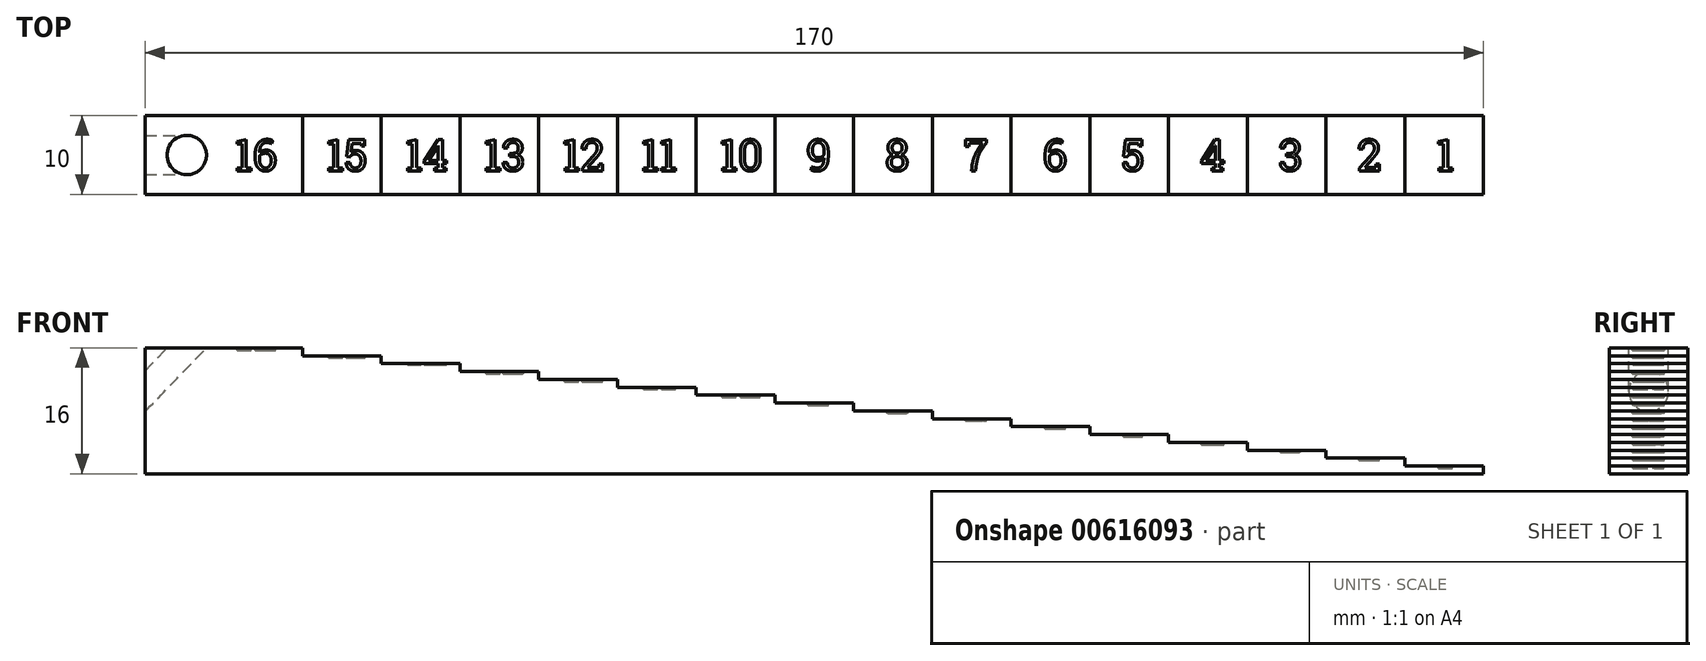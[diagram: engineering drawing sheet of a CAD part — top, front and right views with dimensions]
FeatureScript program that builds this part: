
annotation { "Feature Type Name" : "Feature", "Feature Type Description" : "" }
export const myFeature = defineFeature(function(context is Context, id is Id, definition is map)
    precondition{}
    {
        {
            var Q0;
            Q0=qCreatedBy(makeId("Front.planeOp"),FACE);
            var sketch = newSketch(context, id + "F0", { "sketchPlane" : qUnion([Q0])});
            skLineSegment(sketch, "E0", {"start": v(0, 0) * mm, "end": v(-170, 0) * mm});
            skLineSegment(sketch, "E1", {"start": v(-170, 0) * mm, "end": v(-170, 16) * mm});
            skLineSegment(sketch, "E2", {"start": v(0, 0) * mm, "end": v(0, 1) * mm});
            skLineSegment(sketch, "E3", {"start": v(0, 1) * mm, "end": v(-10, 1) * mm});
            skLineSegment(sketch, "E4", {"start": v(-10, 1) * mm, "end": v(-10, 2) * mm});
            skLineSegment(sketch, "E5", {"start": v(-10, 2) * mm, "end": v(-20, 2) * mm});
            skLineSegment(sketch, "E6", {"start": v(-20, 2) * mm, "end": v(-20, 3) * mm});
            skLineSegment(sketch, "E7", {"start": v(-20, 3) * mm, "end": v(-30, 3) * mm});
            skLineSegment(sketch, "E8", {"start": v(-30, 3) * mm, "end": v(-30, 4) * mm});
            skLineSegment(sketch, "E9", {"start": v(-30, 4) * mm, "end": v(-40, 4) * mm});
            skLineSegment(sketch, "E10", {"start": v(-40, 4) * mm, "end": v(-40, 5) * mm});
            skLineSegment(sketch, "E11", {"start": v(-40, 5) * mm, "end": v(-50, 5) * mm});
            skLineSegment(sketch, "E12", {"start": v(-50, 5) * mm, "end": v(-50, 6) * mm});
            skLineSegment(sketch, "E13", {"start": v(-50, 6) * mm, "end": v(-60, 6) * mm});
            skLineSegment(sketch, "E14", {"start": v(-60, 6) * mm, "end": v(-60, 7) * mm});
            skLineSegment(sketch, "E15", {"start": v(-60, 7) * mm, "end": v(-70, 7) * mm});
            skLineSegment(sketch, "E16", {"start": v(-70, 7) * mm, "end": v(-70, 8) * mm});
            skLineSegment(sketch, "E17", {"start": v(-70, 8) * mm, "end": v(-80, 8) * mm});
            skLineSegment(sketch, "E18", {"start": v(-80, 8) * mm, "end": v(-80, 9) * mm});
            skLineSegment(sketch, "E19", {"start": v(-80, 9) * mm, "end": v(-90, 9) * mm});
            skLineSegment(sketch, "E20", {"start": v(-90, 9) * mm, "end": v(-90, 10) * mm});
            skLineSegment(sketch, "E21", {"start": v(-90, 10) * mm, "end": v(-100, 10) * mm});
            skLineSegment(sketch, "E22", {"start": v(-100, 10) * mm, "end": v(-100, 11) * mm});
            skLineSegment(sketch, "E23", {"start": v(-100, 11) * mm, "end": v(-110, 11) * mm});
            skLineSegment(sketch, "E24", {"start": v(-110, 11) * mm, "end": v(-110, 12) * mm});
            skLineSegment(sketch, "E25", {"start": v(-110, 12) * mm, "end": v(-120, 12) * mm});
            skLineSegment(sketch, "E26", {"start": v(-120, 12) * mm, "end": v(-120, 13) * mm});
            skLineSegment(sketch, "E27", {"start": v(-120, 13) * mm, "end": v(-130, 13) * mm});
            skLineSegment(sketch, "E28", {"start": v(-130, 13) * mm, "end": v(-130, 14) * mm});
            skLineSegment(sketch, "E29", {"start": v(-130, 14) * mm, "end": v(-140, 14) * mm});
            skLineSegment(sketch, "E30", {"start": v(-140, 14) * mm, "end": v(-140, 15) * mm});
            skLineSegment(sketch, "E31", {"start": v(-140, 15) * mm, "end": v(-150, 15) * mm});
            skLineSegment(sketch, "E32", {"start": v(-150, 15) * mm, "end": v(-150, 16) * mm});
            skLineSegment(sketch, "E33", {"start": v(-150, 16) * mm, "end": v(-170, 16) * mm});
            skSolve(sketch);
        }
        {
            var Q0;
            Q0 = qSketchRegion(id + "F0", true);
            extrude(context, id + "F1", {"entities" : qUnion([Q0]), "depth" : 10 * mm, "offsetDistance" : 25 * mm});
        }
        {
            var Q0;
            Q0=makeQuery(id+"F1.opExtrude","SWEPT_FACE",FACE,{"disambiguationData":[OSD([sQuery(id+"F0.wireOp",EDGE,"E3")])]});
            var sketch = newSketch(context, id + "F2", { "sketchPlane" : qUnion([Q0])});
            skText(sketch, "E34", { "text": "1", "fontName": "RobotoSlab-Regular.ttf"});
            const initialGuessF2  = {"E34": [-0.006, -0.007, 1, 0, 0.004]};
            skSetInitialGuess(sketch, initialGuessF2);
            skSolve(sketch);
        }
        {
            var Q0;
            Q0 = qSketchRegion(id + "F2", true);
            extrude(context, id + "F3", {"entities" : qUnion([Q0]), "operationType" : NewBodyOperationType.REMOVE, "oppositeDirection" : true, "depth" : 0.3 * mm, "offsetDistance" : 25 * mm});
        }
        {
            var Q0;
            Q0=makeQuery(id+"F1.opExtrude","SWEPT_FACE",FACE,{"disambiguationData":[OSD([sQuery(id+"F0.wireOp",EDGE,"E5")])]});
            var sketch = newSketch(context, id + "F4", { "sketchPlane" : qUnion([Q0])});
            skText(sketch, "E35", { "text": "2", "fontName": "RobotoSlab-Regular.ttf"});
            const initialGuessF4  = {"E35": [-0.016, -0.007, 1, 0, 0.004]};
            skSetInitialGuess(sketch, initialGuessF4);
            skSolve(sketch);
        }
        {
            var Q0;
            Q0 = qSketchRegion(id + "F4", true);
            extrude(context, id + "F5", {"entities" : qUnion([Q0]), "operationType" : NewBodyOperationType.REMOVE, "oppositeDirection" : true, "depth" : 0.3 * mm, "offsetDistance" : 25 * mm});
        }
        {
            var Q0;
            Q0=makeQuery(id+"F1.opExtrude","SWEPT_FACE",FACE,{"disambiguationData":[OSD([sQuery(id+"F0.wireOp",EDGE,"E7")])]});
            var sketch = newSketch(context, id + "F6", { "sketchPlane" : qUnion([Q0])});
            skText(sketch, "E36", { "text": "3", "fontName": "RobotoSlab-Regular.ttf"});
            const initialGuessF6  = {"E36": [-0.026, -0.007, 1, 0, 0.004]};
            skSetInitialGuess(sketch, initialGuessF6);
            skSolve(sketch);
        }
        {
            var Q0;
            Q0 = qSketchRegion(id + "F6", true);
            extrude(context, id + "F7", {"entities" : qUnion([Q0]), "operationType" : NewBodyOperationType.REMOVE, "oppositeDirection" : true, "depth" : 0.3 * mm, "offsetDistance" : 25 * mm});
        }
        {
            var Q0;
            Q0=makeQuery(id+"F1.opExtrude","SWEPT_FACE",FACE,{"disambiguationData":[OSD([sQuery(id+"F0.wireOp",EDGE,"E9")])]});
            var sketch = newSketch(context, id + "F8", { "sketchPlane" : qUnion([Q0])});
            skText(sketch, "E37", { "text": "4", "fontName": "RobotoSlab-Regular.ttf"});
            const initialGuessF8  = {"E37": [-0.036, -0.007, 1, 0, 0.004]};
            skSetInitialGuess(sketch, initialGuessF8);
            skSolve(sketch);
        }
        {
            var Q0;
            Q0 = qSketchRegion(id + "F8", true);
            extrude(context, id + "F9", {"entities" : qUnion([Q0]), "operationType" : NewBodyOperationType.REMOVE, "oppositeDirection" : true, "depth" : 0.3 * mm, "offsetDistance" : 25 * mm});
        }
        {
            var Q0;
            Q0=makeQuery(id+"F1.opExtrude","SWEPT_FACE",FACE,{"disambiguationData":[OSD([sQuery(id+"F0.wireOp",EDGE,"E11")])]});
            var sketch = newSketch(context, id + "F10", { "sketchPlane" : qUnion([Q0])});
            skText(sketch, "E38", { "text": "5", "fontName": "RobotoSlab-Regular.ttf"});
            const initialGuessF10  = {"E38": [-0.046, -0.007, 1, 0, 0.004]};
            skSetInitialGuess(sketch, initialGuessF10);
            skSolve(sketch);
        }
        {
            var Q0;
            Q0 = qSketchRegion(id + "F10", true);
            extrude(context, id + "F11", {"entities" : qUnion([Q0]), "operationType" : NewBodyOperationType.REMOVE, "oppositeDirection" : true, "depth" : 0.3 * mm, "offsetDistance" : 25 * mm});
        }
        {
            var Q0;
            Q0=makeQuery(id+"F1.opExtrude","SWEPT_FACE",FACE,{"disambiguationData":[OSD([sQuery(id+"F0.wireOp",EDGE,"E13")])]});
            var sketch = newSketch(context, id + "F12", { "sketchPlane" : qUnion([Q0])});
            skText(sketch, "E39", { "text": "6", "fontName": "RobotoSlab-Regular.ttf"});
            const initialGuessF12  = {"E39": [-0.056, -0.007, 1, 0, 0.004]};
            skSetInitialGuess(sketch, initialGuessF12);
            skSolve(sketch);
        }
        {
            var Q0;
            Q0 = qSketchRegion(id + "F12", true);
            extrude(context, id + "F13", {"entities" : qUnion([Q0]), "operationType" : NewBodyOperationType.REMOVE, "oppositeDirection" : true, "depth" : 0.3 * mm, "offsetDistance" : 25 * mm});
        }
        {
            var Q0;
            Q0=makeQuery(id+"F1.opExtrude","SWEPT_FACE",FACE,{"disambiguationData":[OSD([sQuery(id+"F0.wireOp",EDGE,"E15")])]});
            var sketch = newSketch(context, id + "F14", { "sketchPlane" : qUnion([Q0])});
            skText(sketch, "E40", { "text": "7", "fontName": "RobotoSlab-Regular.ttf"});
            const initialGuessF14  = {"E40": [-0.066, -0.007, 1, 0, 0.004]};
            skSetInitialGuess(sketch, initialGuessF14);
            skSolve(sketch);
        }
        {
            var Q0;
            Q0 = qSketchRegion(id + "F14", true);
            extrude(context, id + "F15", {"entities" : qUnion([Q0]), "operationType" : NewBodyOperationType.REMOVE, "oppositeDirection" : true, "depth" : 0.3 * mm, "offsetDistance" : 25 * mm});
        }
        {
            var Q0;
            Q0=makeQuery(id+"F1.opExtrude","SWEPT_FACE",FACE,{"disambiguationData":[OSD([sQuery(id+"F0.wireOp",EDGE,"E17")])]});
            var sketch = newSketch(context, id + "F16", { "sketchPlane" : qUnion([Q0])});
            skText(sketch, "E41", { "text": "8", "fontName": "RobotoSlab-Regular.ttf"});
            const initialGuessF16  = {"E41": [-0.076, -0.007, 1, 0, 0.004]};
            skSetInitialGuess(sketch, initialGuessF16);
            skSolve(sketch);
        }
        {
            var Q0;
            Q0 = qSketchRegion(id + "F16", true);
            extrude(context, id + "F17", {"entities" : qUnion([Q0]), "operationType" : NewBodyOperationType.REMOVE, "oppositeDirection" : true, "depth" : 0.3 * mm, "offsetDistance" : 25 * mm});
        }
        {
            var Q0;
            Q0=makeQuery(id+"F1.opExtrude","SWEPT_FACE",FACE,{"disambiguationData":[OSD([sQuery(id+"F0.wireOp",EDGE,"E19")])]});
            var sketch = newSketch(context, id + "F18", { "sketchPlane" : qUnion([Q0])});
            skText(sketch, "E42", { "text": "9", "fontName": "RobotoSlab-Regular.ttf"});
            const initialGuessF18  = {"E42": [-0.086, -0.007, 1, 0, 0.004]};
            skSetInitialGuess(sketch, initialGuessF18);
            skSolve(sketch);
        }
        {
            var Q0;
            Q0 = qSketchRegion(id + "F18", true);
            extrude(context, id + "F19", {"entities" : qUnion([Q0]), "operationType" : NewBodyOperationType.REMOVE, "oppositeDirection" : true, "depth" : 0.3 * mm, "offsetDistance" : 25 * mm});
        }
        {
            var Q0;
            Q0=makeQuery(id+"F1.opExtrude","SWEPT_FACE",FACE,{"disambiguationData":[OSD([sQuery(id+"F0.wireOp",EDGE,"E21")])]});
            var sketch = newSketch(context, id + "F20", { "sketchPlane" : qUnion([Q0])});
            skText(sketch, "E43", { "text": "10", "fontName": "RobotoSlab-Regular.ttf"});
            const initialGuessF20  = {"E43": [-0.097, -0.007, 1, 0, 0.004]};
            skSetInitialGuess(sketch, initialGuessF20);
            skSolve(sketch);
        }
        {
            var Q0;
            Q0 = qSketchRegion(id + "F20", true);
            extrude(context, id + "F21", {"entities" : qUnion([Q0]), "operationType" : NewBodyOperationType.REMOVE, "oppositeDirection" : true, "depth" : 0.3 * mm, "offsetDistance" : 25 * mm});
        }
        {
            var Q0;
            Q0=makeQuery(id+"F1.opExtrude","SWEPT_FACE",FACE,{"disambiguationData":[OSD([sQuery(id+"F0.wireOp",EDGE,"E23")])]});
            var sketch = newSketch(context, id + "F22", { "sketchPlane" : qUnion([Q0])});
            skText(sketch, "E44", { "text": "11", "fontName": "RobotoSlab-Regular.ttf"});
            const initialGuessF22  = {"E44": [-0.107, -0.007, 1, 0, 0.004]};
            skSetInitialGuess(sketch, initialGuessF22);
            skSolve(sketch);
        }
        {
            var Q0;
            Q0 = qSketchRegion(id + "F22", true);
            extrude(context, id + "F23", {"entities" : qUnion([Q0]), "operationType" : NewBodyOperationType.REMOVE, "oppositeDirection" : true, "depth" : 0.3 * mm, "offsetDistance" : 25 * mm});
        }
        {
            var Q0;
            Q0=makeQuery(id+"F1.opExtrude","SWEPT_FACE",FACE,{"disambiguationData":[OSD([sQuery(id+"F0.wireOp",EDGE,"E25")])]});
            var sketch = newSketch(context, id + "F24", { "sketchPlane" : qUnion([Q0])});
            skText(sketch, "E45", { "text": "12", "fontName": "RobotoSlab-Regular.ttf"});
            const initialGuessF24  = {"E45": [-0.117, -0.007, 1, 0, 0.004]};
            skSetInitialGuess(sketch, initialGuessF24);
            skSolve(sketch);
        }
        {
            var Q0;
            Q0 = qSketchRegion(id + "F24", true);
            extrude(context, id + "F25", {"entities" : qUnion([Q0]), "operationType" : NewBodyOperationType.REMOVE, "oppositeDirection" : true, "depth" : 0.3 * mm, "offsetDistance" : 25 * mm});
        }
        {
            var Q0;
            Q0=makeQuery(id+"F1.opExtrude","SWEPT_FACE",FACE,{"disambiguationData":[OSD([sQuery(id+"F0.wireOp",EDGE,"E27")])]});
            var sketch = newSketch(context, id + "F26", { "sketchPlane" : qUnion([Q0])});
            skText(sketch, "E46", { "text": "13", "fontName": "RobotoSlab-Regular.ttf"});
            const initialGuessF26  = {"E46": [-0.127, -0.007, 1, 0, 0.004]};
            skSetInitialGuess(sketch, initialGuessF26);
            skSolve(sketch);
        }
        {
            var Q0;
            Q0 = qSketchRegion(id + "F26", true);
            extrude(context, id + "F27", {"entities" : qUnion([Q0]), "operationType" : NewBodyOperationType.REMOVE, "oppositeDirection" : true, "depth" : 0.3 * mm, "offsetDistance" : 25 * mm});
        }
        {
            var Q0;
            Q0=makeQuery(id+"F1.opExtrude","SWEPT_FACE",FACE,{"disambiguationData":[OSD([sQuery(id+"F0.wireOp",EDGE,"E29")])]});
            var sketch = newSketch(context, id + "F28", { "sketchPlane" : qUnion([Q0])});
            skText(sketch, "E47", { "text": "14", "fontName": "RobotoSlab-Regular.ttf"});
            const initialGuessF28  = {"E47": [-0.137, -0.007, 1, 0, 0.004]};
            skSetInitialGuess(sketch, initialGuessF28);
            skSolve(sketch);
        }
        {
            var Q0;
            Q0 = qSketchRegion(id + "F28", true);
            extrude(context, id + "F29", {"entities" : qUnion([Q0]), "operationType" : NewBodyOperationType.REMOVE, "oppositeDirection" : true, "depth" : 0.2 * mm, "offsetDistance" : 25 * mm});
        }
        {
            var Q0;
            Q0=makeQuery(id+"F1.opExtrude","SWEPT_FACE",FACE,{"disambiguationData":[OSD([sQuery(id+"F0.wireOp",EDGE,"E31")])]});
            var sketch = newSketch(context, id + "F30", { "sketchPlane" : qUnion([Q0])});
            skText(sketch, "E48", { "text": "15", "fontName": "RobotoSlab-Regular.ttf"});
            skPoint(sketch, "E48.secondSnap0", {"position": v(-141.7, -7.25) * mm});
            const initialGuessF30  = {"E48": [-0.147, -0.007, 1, 0, 0.004]};
            skSetInitialGuess(sketch, initialGuessF30);
            skSolve(sketch);
        }
        {
            var Q0;
            Q0 = qSketchRegion(id + "F30", true);
            extrude(context, id + "F31", {"entities" : qUnion([Q0]), "operationType" : NewBodyOperationType.REMOVE, "oppositeDirection" : true, "depth" : 0.3 * mm, "offsetDistance" : 25 * mm});
        }
        {
            var Q0;
            Q0=makeQuery(id+"F1.opExtrude","SWEPT_FACE",FACE,{"disambiguationData":[OSD([sQuery(id+"F0.wireOp",EDGE,"E33")])]});
            var sketch = newSketch(context, id + "F32", { "sketchPlane" : qUnion([Q0])});
            skText(sketch, "E49", { "text": "16", "fontName": "RobotoSlab-Regular.ttf"});
            const initialGuessF32  = {"E49": [-0.15863, -0.007, 1, 0, 0.004]};
            skSetInitialGuess(sketch, initialGuessF32);
            skSolve(sketch);
        }
        {
            var Q0;
            Q0 = qSketchRegion(id + "F32", true);
            extrude(context, id + "F33", {"entities" : qUnion([Q0]), "operationType" : NewBodyOperationType.REMOVE, "oppositeDirection" : true, "depth" : 0.3 * mm, "offsetDistance" : 25 * mm});
        }
        {
            var Q0;
            {var subQ1=sQuery(id+"F0.wireOp",EDGE,"E33");var subQ32=sQuery(id+"F0.wireOp",EDGE,"E1");Q0=makeQuery(id+"F33.boolean.opBoolean","SPLIT",FACE,{"disambiguationData":[TD([makeQuery(id+"F1.opExtrude","SWEPT_FACE",FACE,{"disambiguationData":[OSD([subQ32])]})])],"derivedFrom":makeQuery(id+"F1.opExtrude","SWEPT_FACE",FACE,{"disambiguationData":[OSD([subQ1])]})});}
            var sketch = newSketch(context, id + "F34", { "sketchPlane" : qUnion([Q0])});
            skCircle(sketch, "E50", {"center": v(-164.7, -5) * mm, "radius": 2.5 * mm});
            skPoint(sketch, "E50.centerSnap0", {"position": v(-170, -5) * mm});
            skSolve(sketch);
        }
        {
            var Q0;
            Q0=makeQuery(id+"F1.opExtrude","CAP_FACE",FACE,{"disambiguationData":[OSD([sQuery(id+"F0.wireOp",EDGE,"E0"),sQuery(id+"F0.wireOp",EDGE,"E1"),sQuery(id+"F0.wireOp",EDGE,"E2"),sQuery(id+"F0.wireOp",EDGE,"E3"),sQuery(id+"F0.wireOp",EDGE,"E4"),sQuery(id+"F0.wireOp",EDGE,"E5"),sQuery(id+"F0.wireOp",EDGE,"E6"),sQuery(id+"F0.wireOp",EDGE,"E7"),sQuery(id+"F0.wireOp",EDGE,"E8"),sQuery(id+"F0.wireOp",EDGE,"E9"),sQuery(id+"F0.wireOp",EDGE,"E10"),sQuery(id+"F0.wireOp",EDGE,"E11"),sQuery(id+"F0.wireOp",EDGE,"E12"),sQuery(id+"F0.wireOp",EDGE,"E13"),sQuery(id+"F0.wireOp",EDGE,"E14"),sQuery(id+"F0.wireOp",EDGE,"E15"),sQuery(id+"F0.wireOp",EDGE,"E16"),sQuery(id+"F0.wireOp",EDGE,"E17"),sQuery(id+"F0.wireOp",EDGE,"E18"),sQuery(id+"F0.wireOp",EDGE,"E19"),sQuery(id+"F0.wireOp",EDGE,"E20"),sQuery(id+"F0.wireOp",EDGE,"E21"),sQuery(id+"F0.wireOp",EDGE,"E22"),sQuery(id+"F0.wireOp",EDGE,"E23"),sQuery(id+"F0.wireOp",EDGE,"E24"),sQuery(id+"F0.wireOp",EDGE,"E25"),sQuery(id+"F0.wireOp",EDGE,"E26"),sQuery(id+"F0.wireOp",EDGE,"E27"),sQuery(id+"F0.wireOp",EDGE,"E28"),sQuery(id+"F0.wireOp",EDGE,"E29"),sQuery(id+"F0.wireOp",EDGE,"E30"),sQuery(id+"F0.wireOp",EDGE,"E31"),sQuery(id+"F0.wireOp",EDGE,"E32"),sQuery(id+"F0.wireOp",EDGE,"E33")])],"isStart":false});
            var Q1;
            Q1=makeQuery(id+"F1.opExtrude","CAP_FACE",FACE,{"disambiguationData":[OSD([sQuery(id+"F0.wireOp",EDGE,"E0"),sQuery(id+"F0.wireOp",EDGE,"E1"),sQuery(id+"F0.wireOp",EDGE,"E2"),sQuery(id+"F0.wireOp",EDGE,"E3"),sQuery(id+"F0.wireOp",EDGE,"E4"),sQuery(id+"F0.wireOp",EDGE,"E5"),sQuery(id+"F0.wireOp",EDGE,"E6"),sQuery(id+"F0.wireOp",EDGE,"E7"),sQuery(id+"F0.wireOp",EDGE,"E8"),sQuery(id+"F0.wireOp",EDGE,"E9"),sQuery(id+"F0.wireOp",EDGE,"E10"),sQuery(id+"F0.wireOp",EDGE,"E11"),sQuery(id+"F0.wireOp",EDGE,"E12"),sQuery(id+"F0.wireOp",EDGE,"E13"),sQuery(id+"F0.wireOp",EDGE,"E14"),sQuery(id+"F0.wireOp",EDGE,"E15"),sQuery(id+"F0.wireOp",EDGE,"E16"),sQuery(id+"F0.wireOp",EDGE,"E17"),sQuery(id+"F0.wireOp",EDGE,"E18"),sQuery(id+"F0.wireOp",EDGE,"E19"),sQuery(id+"F0.wireOp",EDGE,"E20"),sQuery(id+"F0.wireOp",EDGE,"E21"),sQuery(id+"F0.wireOp",EDGE,"E22"),sQuery(id+"F0.wireOp",EDGE,"E23"),sQuery(id+"F0.wireOp",EDGE,"E24"),sQuery(id+"F0.wireOp",EDGE,"E25"),sQuery(id+"F0.wireOp",EDGE,"E26"),sQuery(id+"F0.wireOp",EDGE,"E27"),sQuery(id+"F0.wireOp",EDGE,"E28"),sQuery(id+"F0.wireOp",EDGE,"E29"),sQuery(id+"F0.wireOp",EDGE,"E30"),sQuery(id+"F0.wireOp",EDGE,"E31"),sQuery(id+"F0.wireOp",EDGE,"E32"),sQuery(id+"F0.wireOp",EDGE,"E33")])],"isStart":true});
            cPlane(context, id + "F35", {"entities" : qUnion([Q0, Q1]), "cplaneType" : CPlaneType.MID_PLANE, "offset" : 25 * mm, "width" : 150 * mm, "height" : 150 * mm});
        }
        {
            var Q0;
            Q0=qCreatedBy(id+"F35.planeOp",FACE);
            var sketch = newSketch(context, id + "F36", { "sketchPlane" : qUnion([Q0])});
            skLineSegment(sketch, "E51", {"start": v(-164.7, 16) * mm, "end": v(-174.44, 5.88) * mm});
            skSolve(sketch);
        }
        {
            var Q0;
            Q0=makeQuery(id+"F34.imprint","IMPRINT",FACE,{"disambiguationData":[TD([[makeQuery(id+"F34.imprint","IMPRINT",EDGE,{"derivedFrom":sQuery(id+"F34.wireOp",EDGE,"E50")}),1.0]])]});
            var Q1;
            Q1=sQuery(id+"F36.wireOp",EDGE,"E51");
            sweep(context, id + "F37", {"operationType" : NewBodyOperationType.REMOVE, "profiles" : qUnion([Q0]), "path" : qUnion([Q1])});
        }
    });
